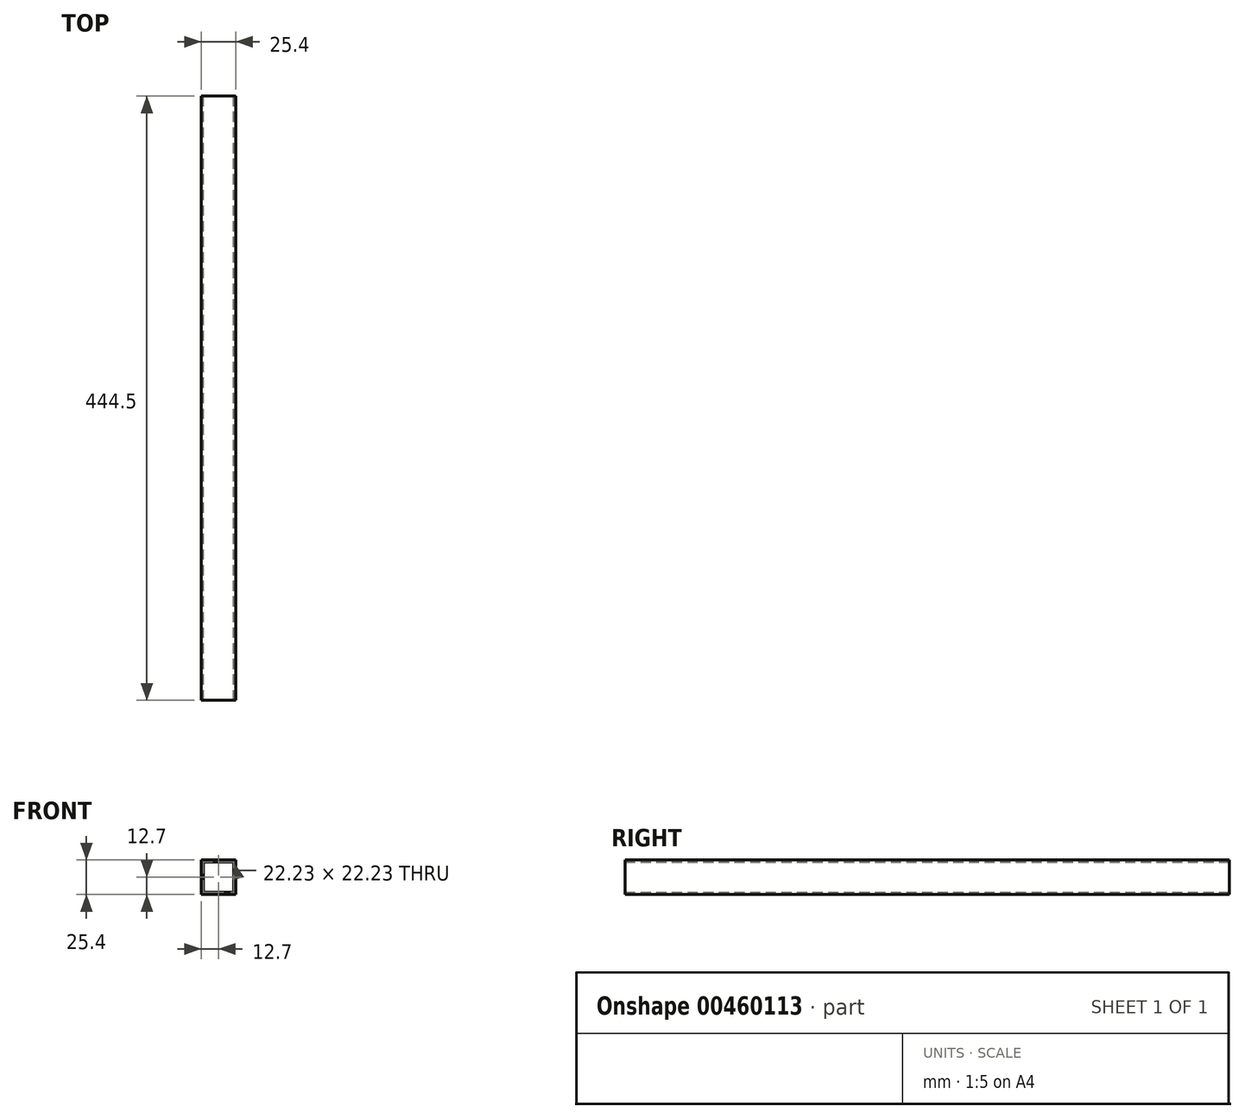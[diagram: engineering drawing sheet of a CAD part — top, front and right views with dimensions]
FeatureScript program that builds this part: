
annotation { "Feature Type Name" : "Feature", "Feature Type Description" : "" }
export const myFeature = defineFeature(function(context is Context, id is Id, definition is map)
    precondition{}
    {
        {
            var Q0;
            Q0=qCreatedBy(makeId("Front.planeOp"),FACE);
            var sketch = newSketch(context, id + "F0", { "sketchPlane" : qUnion([Q0])});
            skLineSegment(sketch, "E0.bottom", {"start": v(12.7, 12.7) * mm, "end": v(-12.7, 12.7) * mm});
            skLineSegment(sketch, "E0.top", {"start": v(12.7, -12.7) * mm, "end": v(-12.7, -12.7) * mm});
            skLineSegment(sketch, "E0.left", {"start": v(12.7, 12.7) * mm, "end": v(12.7, -12.7) * mm});
            skLineSegment(sketch, "E0.right", {"start": v(-12.7, 12.7) * mm, "end": v(-12.7, -12.7) * mm});
            skPoint(sketch, "E0.middle", {"position": v(0, 0) * mm});
            skLineSegment(sketch, "E1.bottom", {"start": v(11.11, 11.11) * mm, "end": v(-11.11, 11.11) * mm});
            skLineSegment(sketch, "E1.top", {"start": v(11.11, -11.11) * mm, "end": v(-11.11, -11.11) * mm});
            skLineSegment(sketch, "E1.left", {"start": v(11.11, 11.11) * mm, "end": v(11.11, -11.11) * mm});
            skLineSegment(sketch, "E1.right", {"start": v(-11.11, 11.11) * mm, "end": v(-11.11, -11.11) * mm});
            skSolve(sketch);
        }
        {
            var Q0;
            Q0=makeQuery(id+"F0.imprint","IMPRINT",FACE,{"disambiguationData":[TD([[makeQuery(id+"F0.imprint","IMPRINT",EDGE,{"derivedFrom":sQuery(id+"F0.wireOp",EDGE,"E0.bottom")}),1.0]])]});
            extrude(context, id + "F1", {"entities" : qUnion([Q0]), "depth" : 444.5 * mm});
        }
    });
